# Revit family: Porta CF manual com PT
name_source: partatom
category: Doors
units: mm (PartAtom-declared; Revit-internal decimal feet)

## family parameters
Cut with Voids When Loaded = Yes
Host = Face
Room Calculation Point = No
Shared = No

## types (3) — shared parameters
Automatica = No
Define Thermal Properties by = Schematic Type
Dist Motor = 30 mm  [stored 0.0984252 ft]
Manual = Yes
NaN = Yes
zero-valued in all types: Default Elevation

## per-type parameters (varying)
| type | Altura PT | Altura Vao Luz | Altura trilho superior | Desloc Lateral PT | Desloc PT | Height | Largura PT | Largura Vao Luz | Thickness | Width |
| 1500 x 2200 x 150 mm | 758 mm  [stored 2.48688 ft] | 2200 mm | 1020 mm  [stored 3.34646 ft] | 750 mm  [stored 2.46063 ft] | 0 mm  [stored 0 ft] | 2200 mm | 340 mm  [stored 1.11549 ft] | 1500 mm  [stored 4.92126 ft] | 150 mm  [stored 0.492126 ft] | 1500 mm  [stored 4.92126 ft] |
| 2000 x 2500 x 100 mm | 540 mm  [stored 1.77165 ft] | 2500 mm  [stored 8.2021 ft] | 802 mm  [stored 2.63123 ft] | 1750 mm  [stored 5.74147 ft] | 0 mm  [stored 0 ft] | 2500 mm  [stored 8.2021 ft] | 340 mm  [stored 1.11549 ft] | 3500 mm  [stored 11.4829 ft] | 100 mm  [stored 0.328084 ft] | 3500 mm  [stored 11.4829 ft] |
| 1000 x 2200 x 150 mm | 148 mm | 2200 mm | 410 mm  [stored 1.34514 ft] | 2074 mm | 1574 mm | 2200 mm | 803 mm | 1000 mm  [stored 3.28084 ft] | 150 mm  [stored 0.492126 ft] | 1000 mm  [stored 3.28084 ft] |

note: [stored X ft] marks values corroborated as IEEE doubles in the binary element streams (Revit-internal decimal feet)

## geometry (parser evidence)
native form markers: Blend x2
no freeform markers — native parametric forms only
